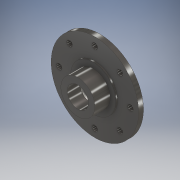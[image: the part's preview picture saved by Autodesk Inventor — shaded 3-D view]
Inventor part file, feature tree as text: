
AUTODESK INVENTOR PART (.ipt)
format: ipt  version: 2017 (Build 210142000, 142)  size: 168,960 bytes
history: native  units: mm
features: extrude x6, sketch x6, fillet x1
ambient origin geometry x8: Origin, YZ Plane, XZ Plane, XY Plane, X Axis, Y Axis, Z Axis, Center Point
bodies: Solid1 (feature_tree)
feature tree (13):
  extrude  "Extrusion1"  Depth=3.0mm TaperAngle=0.0deg
  extrude  "Extrusion2"  Depth=1.5mm TaperAngle=0.0deg
  extrude  "Extrusion3"  Depth=1.0mm TaperAngle=0.0deg
  extrude  "Extrusion4"  Depth=1.0mm TaperAngle=0.0deg
  extrude  "Extrusion6"  Depth=9.5mm
  fillet  "Fillet1"  Radius=9.5mm
  extrude  "Extrusion7"  Depth=2.0mm
  sketch  "Sketch1"  dims[d0=54.0mm d1=3.0mm d2=0.0mm]
  sketch  "Sketch2"  dims[d3=32.0mm d4=1.5mm d5=0.0mm]
  sketch  "Sketch3"  dims[d6=28.0mm d7=1.0mm d8=0.0mm]
  sketch  "Sketch4"  dims[d9=6.0mm d10=1.0mm d11=0.0mm]
  sketch  "Sketch5"  dims[d12=13.0mm d16=21.0mm d17=9.5mm d18=0.0mm]
  sketch  "Sketch7"  dims[d19=2.0mm d20=44.0mm d22=3.5mm d23=80.0mm d25=360.0deg d27=0.0mm d28=0.0mm]
